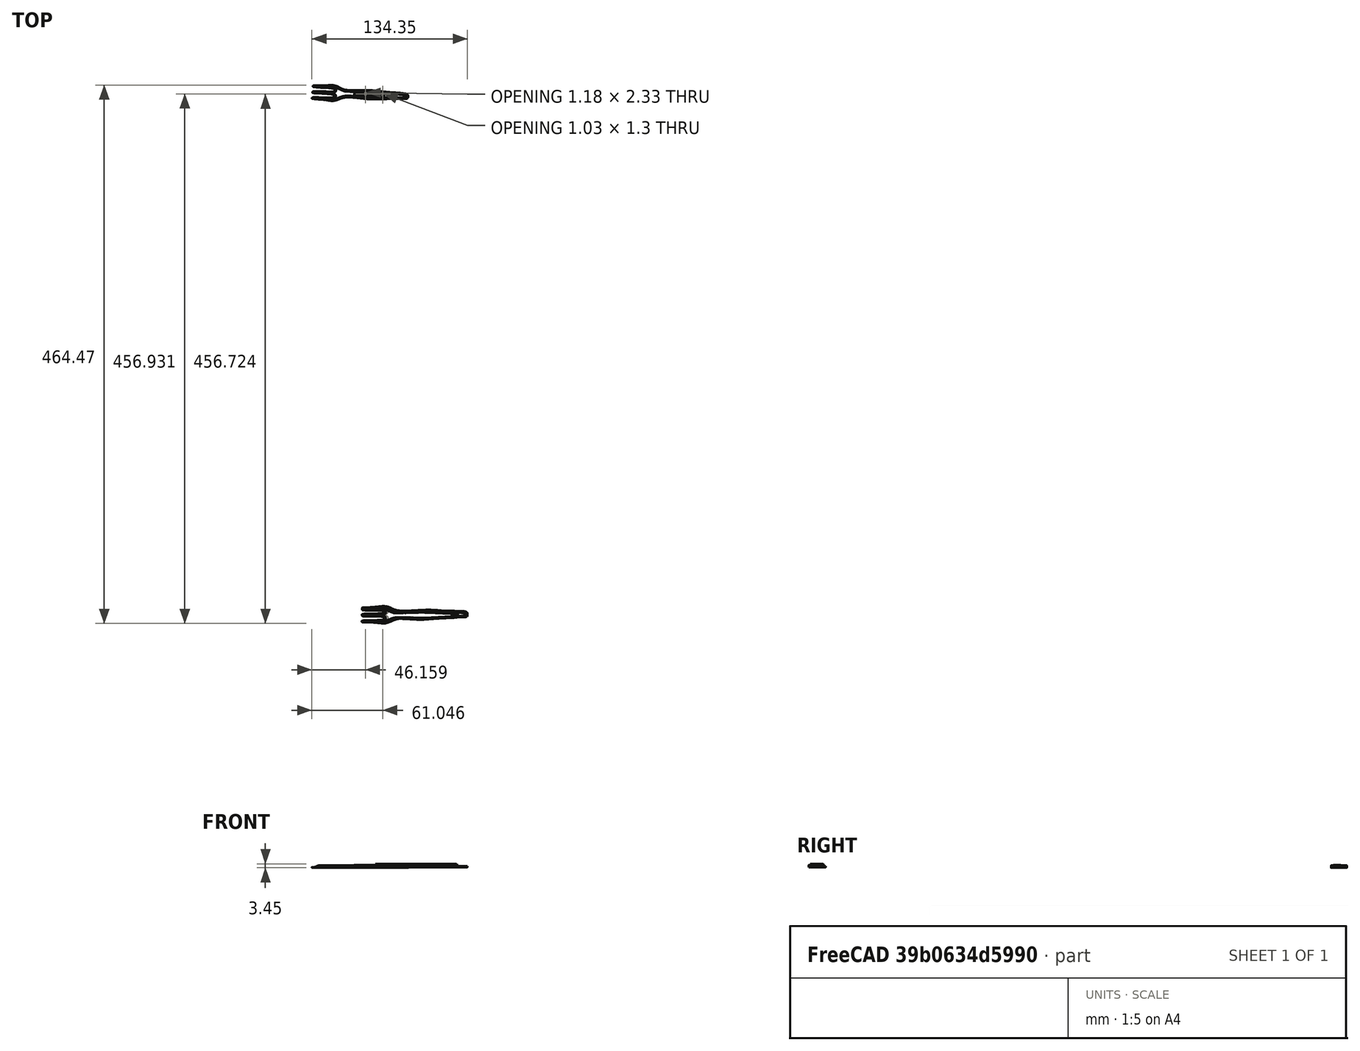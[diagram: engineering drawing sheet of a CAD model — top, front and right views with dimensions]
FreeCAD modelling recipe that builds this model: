
FCSTD DOCUMENT  (FreeCAD 0.15R4671 (Git))
Label: tenedor_v2
License: All rights reserved
LicenseURL: http://es.wikipedia.org/wiki/Todos_los_derechos_reservados
objects: Part::Extrusion×7, Part::Feature×5, Part::Cut×3, Part::Cylinder×1, Part::Fillet×1, Part::Part2DObjectPython×1, Part::MultiFuse×1
note: 19 computed .brp shape members not serialized (recipe doc carries the construction recipe); baked Part::Feature solids carry a one-line shape summary decoded from their .brp

FEATURE [Part::Feature] path4209
  shape: bbox 91.47 x 14.87 x 2e-07 mm, 0 faces, 0 solids (baked)
FEATURE [Part::Feature] path4209001
  shape: bbox 76.61 x 12.54 x 2e-07 mm, 0 faces, 0 solids (baked)
FEATURE [Part::Extrusion] Extrude
  Base = -> path4209001
  Dir = (0,0,1)
  Placement = pos=(0,0,0.5) rot=(0,0,1;0rad)
  Solid = true
FEATURE [Part::Extrusion] Extrude001
  Base = -> path4209
  Dir = (0,0,1)
  Solid = true
FEATURE [Part::Cut] Cut
  Base = -> Extrude001
  Tool = -> Extrude
FEATURE [Part::Feature] path4209002
  shape: bbox 83.21 x 13.57 x 2e-07 mm, 0 faces, 0 solids (baked)
FEATURE [Part::Feature] path4209003
  shape: bbox 70.23 x 11.17 x 2e-07 mm, 0 faces, 0 solids (baked)
FEATURE [Part::Extrusion] Extrude002
  Base = -> path4209003
  Dir = (0,0,2)
  Placement = pos=(0,0,1) rot=(0,0,1;0rad)
  Solid = true
FEATURE [Part::Extrusion] Extrude003
  Base = -> path4209003
  Dir = (0,0,2)
  Placement = pos=(0,0,1) rot=(0,0,1;0rad)
  Solid = true
FEATURE [Part::Extrusion] Extrude004
  Base = -> path4209002
  Dir = (0,0,2)
  Solid = true
FEATURE [Part::Extrusion] Extrude005
  Base = -> path4209002
  Dir = (0,0,2)
  Solid = true
FEATURE [Part::Cut] Cut001
  Base = -> Extrude004
  Tool = -> Extrude002
FEATURE [Part::Feature] Cut001001  label="Cut002"
  Placement = pos=(-20.5774,451.116,-0.448864) rot=(0,0,-1;0.050054rad)
  shape: bbox 83.38 x 13.6 x 2 mm, 110 faces (baked)
FEATURE [Part::Cylinder] Cylinder  label="Cilindro"
  Angle = 360
  Height = 16
  Placement = pos=(-42,-3,7) rot=(-1,0,0;1.5708rad)
  Radius = 7
FEATURE [Part::Cut] Cut001002
  Base = -> Cut001001
  Tool = -> Cylinder
FEATURE [Part::Fillet] Fillet
  Base = -> Cut001002
  Edges = 3 edges r=6: [Edge67,Edge75,Edge110]
FEATURE [Part::Part2DObjectPython] ShapeString  # Draft 2D object (typed FeaturePython)
  FontFile = <userpath>/Descargas/fonts/Open_Sans/OpenSans-ExtraBold.ttf
  Placement = pos=(-17,0,0) rot=(0,0,1;0rad)
  Size = 7
  String = MAKER
  Tracking = 0
FEATURE [Part::Extrusion] Extrude007
  Base = -> ShapeString
  Dir = (0,0,1)
  Placement = pos=(9.99848,0.674524,1) rot=(0,0,-1;0.034907rad)
  Solid = true
FEATURE [Part::MultiFuse] Fusion
  Shapes = -> [Fillet,Extrude007]
